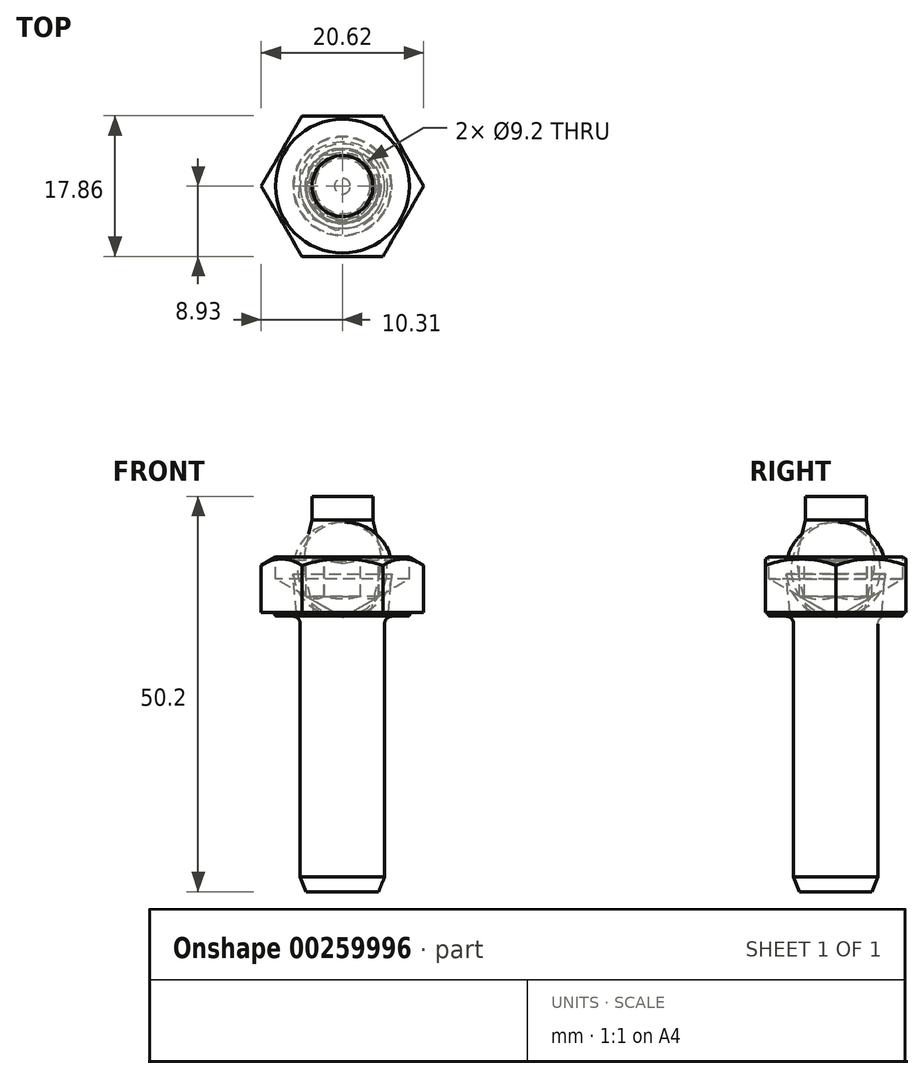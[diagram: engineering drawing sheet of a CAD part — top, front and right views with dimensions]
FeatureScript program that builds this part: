
annotation { "Feature Type Name" : "Feature", "Feature Type Description" : "" }
export const myFeature = defineFeature(function(context is Context, id is Id, definition is map)
    precondition{}
    {
        {
            var Q0;
            Q0=qCreatedBy(makeId("Front.planeOp"),FACE);
            var sketch = newSketch(context, id + "F0", { "sketchPlane" : qUnion([Q0])});
            skLineSegment(sketch, "E0", {"start": v(0, 0) * mm, "end": v(0, 0.42) * mm, "construction": true});
            skLineSegment(sketch, "E1", {"start": v(4.6, 7.5) * mm, "end": v(8.5, 7.5) * mm});
            skLineSegment(sketch, "E2", {"start": v(10.5, 6.35) * mm, "end": v(10.5, 0.5) * mm});
            skLineSegment(sketch, "E3", {"start": v(8.5, 0) * mm, "end": v(5.36, 0) * mm});
            skPoint(sketch, "E4.visualSharp", {"position": v(10.5, 7.5) * mm});
            skLineSegment(sketch, "E5", {"start": v(4.6, 7.5) * mm, "end": v(4.6, 2.5) * mm});
            skLineSegment(sketch, "E6", {"start": v(4.6, 2.5) * mm, "end": v(1, 0.42) * mm});
            skLineSegment(sketch, "E7", {"start": v(1, 0.42) * mm, "end": v(0, 0.42) * mm});
            skLineSegment(sketch, "E8", {"start": v(0, 0.42) * mm, "end": v(0, 0) * mm});
            skLineSegment(sketch, "E9", {"start": v(8.5, 7.5) * mm, "end": v(10.5, 6.35) * mm});
            skLineSegment(sketch, "E10", {"start": v(8.5, 0) * mm, "end": v(8.63, 0.5) * mm});
            skLineSegment(sketch, "E11", {"start": v(8.63, 0.5) * mm, "end": v(10.5, 0.5) * mm});
            skLineSegment(sketch, "E12", {"start": v(0, 0) * mm, "end": v(0, -35) * mm});
            skLineSegment(sketch, "E13", {"start": v(5.36, -33.13) * mm, "end": v(5.36, 0) * mm});
            skLineSegment(sketch, "E14", {"start": v(5.36, -33.13) * mm, "end": v(4.6, -35) * mm});
            skLineSegment(sketch, "E15", {"start": v(4.6, -35) * mm, "end": v(0, -35) * mm});
            skSolve(sketch);
        }
        {
            var Q0;
            Q0=qSketchRegion(id+"F0",true);
            var Q1;
            Q1=sQuery(id+"F0.wireOp",EDGE,"E8");
            revolve(context, id + "F1", {"entities" : qUnion([Q0]), "axis" : qUnion([Q1]), "revolveType" : RevolveType.FULL});
        }
        {
            var Q0;
            Q0=makeQuery(id+"F1.opRevolve","SWEPT_FACE",FACE,{"disambiguationData":[OSD([sQuery(id+"F0.wireOp",EDGE,"E1")])]});
            var sketch = newSketch(context, id + "F2", { "sketchPlane" : qUnion([Q0])});
            skCircle(sketch, "E16", {"center": v(0, 0) * mm, "radius": 4.6 * mm});
            skCircle(sketch, "E17.cCircle", {"center": v(0, 0) * mm, "radius": 4 * mm, "construction": true});
            skLineSegment(sketch, "E17.0", {"start": v(-2.3, 4) * mm, "end": v(2.3, 4) * mm});
            skLineSegment(sketch, "E17.1", {"start": v(2.3, 4) * mm, "end": v(4.62, 0) * mm});
            skLineSegment(sketch, "E17.2", {"start": v(4.62, 0) * mm, "end": v(2.3, -4) * mm});
            skLineSegment(sketch, "E17.3", {"start": v(2.3, -4) * mm, "end": v(-2.3, -4) * mm});
            skLineSegment(sketch, "E17.4", {"start": v(-2.3, -4) * mm, "end": v(-4.62, 0) * mm});
            skLineSegment(sketch, "E17.5", {"start": v(-4.62, 0) * mm, "end": v(-2.3, 4) * mm});
            skPoint(sketch, "E17.0.midPoint", {"position": v(0, 4) * mm});
            skSolve(sketch);
        }
        {
            var Q0;
            {var subQ0=sQuery(id+"F2.wireOp",EDGE,"E17.1");var subQ1=sQuery(id+"F2.wireOp",EDGE,"E16");var subQ2=makeQuery(id+"F2.imprint","INTERSECT",VERTEX,{"disambiguationData":[OD(0.0)],"derivedFrom":[subQ1,subQ0]});Q0=makeQuery(id+"F2.imprint","IMPRINT",FACE,{"disambiguationData":[TD([[makeQuery(id+"F2.imprint","IMPRINT",EDGE,{"disambiguationData":[TD([[subQ2,1.0]])],"derivedFrom":subQ1}),1.0]])]});}
            var Q1;
            {var subQ0=sQuery(id+"F2.wireOp",EDGE,"E17.1");var subQ1=sQuery(id+"F2.wireOp",EDGE,"E16");var subQ2=makeQuery(id+"F2.imprint","INTERSECT",VERTEX,{"disambiguationData":[OD(0.0)],"derivedFrom":[subQ1,subQ0]});Q1=makeQuery(id+"F2.imprint","IMPRINT",FACE,{"disambiguationData":[TD([[makeQuery(id+"F2.imprint","IMPRINT",EDGE,{"disambiguationData":[TD([[subQ2,-1.0]])],"derivedFrom":subQ1}),-1.0]])]});}
            var Q2;
            {var subQ0=sQuery(id+"F2.wireOp",EDGE,"E17.0");var subQ1=sQuery(id+"F2.wireOp",EDGE,"E16");var subQ2=makeQuery(id+"F2.imprint","INTERSECT",VERTEX,{"disambiguationData":[OD(0.0)],"derivedFrom":[subQ1,subQ0]});Q2=makeQuery(id+"F2.imprint","IMPRINT",FACE,{"disambiguationData":[TD([[makeQuery(id+"F2.imprint","IMPRINT",EDGE,{"disambiguationData":[TD([[subQ2,-1.0]])],"derivedFrom":subQ1}),1.0]])]});}
            var Q3;
            {var subQ0=sQuery(id+"F2.wireOp",EDGE,"E17.0");var subQ1=sQuery(id+"F2.wireOp",EDGE,"E16");var subQ2=makeQuery(id+"F2.imprint","INTERSECT",VERTEX,{"disambiguationData":[OD(1.0)],"derivedFrom":[subQ1,subQ0]});Q3=makeQuery(id+"F2.imprint","IMPRINT",FACE,{"disambiguationData":[TD([[makeQuery(id+"F2.imprint","IMPRINT",EDGE,{"disambiguationData":[TD([[subQ2,-1.0]])],"derivedFrom":subQ1}),-1.0]])]});}
            var Q4;
            {var subQ0=sQuery(id+"F2.wireOp",EDGE,"E17.5");var subQ1=sQuery(id+"F2.wireOp",EDGE,"E16");var subQ2=makeQuery(id+"F2.imprint","INTERSECT",VERTEX,{"disambiguationData":[OD(0.0)],"derivedFrom":[subQ1,subQ0]});Q4=makeQuery(id+"F2.imprint","IMPRINT",FACE,{"disambiguationData":[TD([[makeQuery(id+"F2.imprint","IMPRINT",EDGE,{"disambiguationData":[TD([[subQ2,-1.0]])],"derivedFrom":subQ1}),1.0]])]});}
            var Q5;
            {var subQ0=sQuery(id+"F2.wireOp",EDGE,"E17.5");var subQ1=sQuery(id+"F2.wireOp",EDGE,"E16");var subQ2=makeQuery(id+"F2.imprint","INTERSECT",VERTEX,{"disambiguationData":[OD(1.0)],"derivedFrom":[subQ1,subQ0]});Q5=makeQuery(id+"F2.imprint","IMPRINT",FACE,{"disambiguationData":[TD([[makeQuery(id+"F2.imprint","IMPRINT",EDGE,{"disambiguationData":[TD([[subQ2,-1.0]])],"derivedFrom":subQ1}),-1.0]])]});}
            var Q6;
            {var subQ0=sQuery(id+"F2.wireOp",EDGE,"E17.4");var subQ1=sQuery(id+"F2.wireOp",EDGE,"E16");var subQ2=makeQuery(id+"F2.imprint","INTERSECT",VERTEX,{"disambiguationData":[OD(0.0)],"derivedFrom":[subQ1,subQ0]});Q6=makeQuery(id+"F2.imprint","IMPRINT",FACE,{"disambiguationData":[TD([[makeQuery(id+"F2.imprint","IMPRINT",EDGE,{"disambiguationData":[TD([[subQ2,-1.0]])],"derivedFrom":subQ1}),1.0]])]});}
            var Q7;
            {var subQ0=sQuery(id+"F2.wireOp",EDGE,"E17.4");var subQ1=sQuery(id+"F2.wireOp",EDGE,"E16");var subQ2=makeQuery(id+"F2.imprint","INTERSECT",VERTEX,{"disambiguationData":[OD(1.0)],"derivedFrom":[subQ1,subQ0]});Q7=makeQuery(id+"F2.imprint","IMPRINT",FACE,{"disambiguationData":[TD([[makeQuery(id+"F2.imprint","IMPRINT",EDGE,{"disambiguationData":[TD([[subQ2,-1.0]])],"derivedFrom":subQ1}),-1.0]])]});}
            var Q8;
            {var subQ0=sQuery(id+"F2.wireOp",EDGE,"E17.3");var subQ1=sQuery(id+"F2.wireOp",EDGE,"E16");var subQ2=makeQuery(id+"F2.imprint","INTERSECT",VERTEX,{"disambiguationData":[OD(0.0)],"derivedFrom":[subQ1,subQ0]});Q8=makeQuery(id+"F2.imprint","IMPRINT",FACE,{"disambiguationData":[TD([[makeQuery(id+"F2.imprint","IMPRINT",EDGE,{"disambiguationData":[TD([[subQ2,-1.0]])],"derivedFrom":subQ1}),1.0]])]});}
            var Q9;
            {var subQ0=sQuery(id+"F2.wireOp",EDGE,"E17.3");var subQ1=sQuery(id+"F2.wireOp",EDGE,"E16");var subQ2=makeQuery(id+"F2.imprint","INTERSECT",VERTEX,{"disambiguationData":[OD(1.0)],"derivedFrom":[subQ1,subQ0]});Q9=makeQuery(id+"F2.imprint","IMPRINT",FACE,{"disambiguationData":[TD([[makeQuery(id+"F2.imprint","IMPRINT",EDGE,{"disambiguationData":[TD([[subQ2,-1.0]])],"derivedFrom":subQ1}),-1.0]])]});}
            var Q10;
            {var subQ0=sQuery(id+"F2.wireOp",EDGE,"E17.2");var subQ1=sQuery(id+"F2.wireOp",EDGE,"E16");var subQ2=makeQuery(id+"F2.imprint","INTERSECT",VERTEX,{"disambiguationData":[OD(0.0)],"derivedFrom":[subQ1,subQ0]});Q10=makeQuery(id+"F2.imprint","IMPRINT",FACE,{"disambiguationData":[TD([[makeQuery(id+"F2.imprint","IMPRINT",EDGE,{"disambiguationData":[TD([[subQ2,-1.0]])],"derivedFrom":subQ1}),1.0]])]});}
            var Q11;
            {var subQ0=sQuery(id+"F2.wireOp",EDGE,"E17.1");var subQ1=sQuery(id+"F2.wireOp",EDGE,"E16");var subQ2=makeQuery(id+"F2.imprint","INTERSECT",VERTEX,{"disambiguationData":[OD(1.0)],"derivedFrom":[subQ1,subQ0]});Q11=makeQuery(id+"F2.imprint","IMPRINT",FACE,{"disambiguationData":[TD([[makeQuery(id+"F2.imprint","IMPRINT",EDGE,{"disambiguationData":[TD([[subQ2,1.0]])],"derivedFrom":subQ1}),-1.0]])]});}
            var Q12;
            Q12=makeQuery(id+"F1.opRevolve","SWEPT_FACE",FACE,{"disambiguationData":[OSD([sQuery(id+"F0.wireOp",EDGE,"E6")])]});
            extrude(context, id + "F3", {"entities" : qUnion([Q0, Q1, Q2, Q3, Q4, Q5, Q6, Q7, Q8, Q9, Q10, Q11]), "operationType" : NewBodyOperationType.ADD, "endBound" : BoundingType.UP_TO_SURFACE, "oppositeDirection" : true, "endBoundEntityFace" : qUnion([Q12]), "depth" : 25 * mm});
        }
        {
            var Q0;
            Q0=makeQuery(id+"F3.boolean.opBoolean","MERGE",FACE,{"derivedFrom":[makeQuery(id+"F1.opRevolve","SWEPT_FACE",FACE,{"disambiguationData":[OSD([sQuery(id+"F0.wireOp",EDGE,"E1")])]}),makeQuery(id+"F3.opExtrude","CAP_FACE",FACE,{"disambiguationData":[OSD([sQuery(id+"F2.wireOp",EDGE,"axiUSiGf-8ymJ-Ezfh-tHsk-ULXXzRlxOoBz"),sQuery(id+"F2.wireOp",EDGE,"WrdyBTnM-XU54-uk96-2Sjo-h1HHDxb1zyqn"),sQuery(id+"F2.wireOp",EDGE,"7iNK7enz-fUzD-7EQp-KRCh-aPKnPlRcPdaK"),sQuery(id+"F2.wireOp",EDGE,"e7c95674-c634-4135-8625-61586754ee6a.1.0"),sQuery(id+"F2.wireOp",EDGE,"e7c95674-c634-4135-8625-61586754ee6a.1.1"),sQuery(id+"F2.wireOp",EDGE,"e7c95674-c634-4135-8625-61586754ee6a.1.2"),sQuery(id+"F2.wireOp",EDGE,"e7c95674-c634-4135-8625-61586754ee6a.2.0"),sQuery(id+"F2.wireOp",EDGE,"e7c95674-c634-4135-8625-61586754ee6a.2.1"),sQuery(id+"F2.wireOp",EDGE,"e7c95674-c634-4135-8625-61586754ee6a.2.2"),sQuery(id+"F2.wireOp",EDGE,"e7c95674-c634-4135-8625-61586754ee6a.3.0"),sQuery(id+"F2.wireOp",EDGE,"e7c95674-c634-4135-8625-61586754ee6a.3.1"),sQuery(id+"F2.wireOp",EDGE,"e7c95674-c634-4135-8625-61586754ee6a.3.2"),sQuery(id+"F2.wireOp",EDGE,"e7c95674-c634-4135-8625-61586754ee6a.4.0"),sQuery(id+"F2.wireOp",EDGE,"e7c95674-c634-4135-8625-61586754ee6a.4.1"),sQuery(id+"F2.wireOp",EDGE,"e7c95674-c634-4135-8625-61586754ee6a.4.2"),sQuery(id+"F2.wireOp",EDGE,"e7c95674-c634-4135-8625-61586754ee6a.5.0"),sQuery(id+"F2.wireOp",EDGE,"e7c95674-c634-4135-8625-61586754ee6a.5.1"),sQuery(id+"F2.wireOp",EDGE,"e7c95674-c634-4135-8625-61586754ee6a.5.2"),sQuery(id+"F2.wireOp",EDGE,"c34f7dbc-1fd9-48ae-9599-0fb72b0d65de.filletArc"),sQuery(id+"F2.wireOp",EDGE,"5fecc0f4-c57f-42b8-a97f-f8fbf54cf4db.filletArc"),sQuery(id+"F2.wireOp",EDGE,"b077568f-b672-48a6-a184-fa18c1575088.filletArc"),sQuery(id+"F2.wireOp",EDGE,"4c4ba650-eb3b-40a6-a5b6-7d0bcd232093.filletArc"),sQuery(id+"F2.wireOp",EDGE,"b016cc09-0b8d-437b-9508-1d7630c9d4ff.filletArc"),sQuery(id+"F2.wireOp",EDGE,"d5479cb3-145b-41e2-b586-5ab3f6452500.filletArc"),sQuery(id+"F2.wireOp",EDGE,"E16")])],"isStart":true})]});
            var sketch = newSketch(context, id + "F4", { "sketchPlane" : qUnion([Q0])});
            skCircle(sketch, "E18", {"center": v(0, 0) * mm, "radius": 4.75 * mm});
            skSolve(sketch);
        }
        {
            var Q0;
            Q0=qSketchRegion(id+"F4",true);
            extrude(context, id + "F5", {"entities" : qUnion([Q0]), "operationType" : NewBodyOperationType.REMOVE, "oppositeDirection" : true, "depth" : 1 * mm, "hasDraft" : true, "draftAngle" : 80 * degree, "draftPullDirection" : true});
        }
        {
            var Q0;
            {var subQ0=sQuery(id+"F2.wireOp",EDGE,"E16");Q0=makeQuery(id+"F3.boolean.opBoolean","MERGE",FACE,{"derivedFrom":[makeQuery(id+"F1.opRevolve","SWEPT_FACE",FACE,{"disambiguationData":[OSD([sQuery(id+"F0.wireOp",EDGE,"E1")])]}),makeQuery(id+"F3.opExtrude","CAP_FACE",FACE,{"disambiguationData":[OSD([subQ0,sQuery(id+"F2.wireOp",EDGE,"E17.1")])],"isStart":true}),makeQuery(id+"F3.opExtrude","CAP_FACE",FACE,{"disambiguationData":[OSD([subQ0,sQuery(id+"F2.wireOp",EDGE,"E17.0")])],"isStart":true}),makeQuery(id+"F3.opExtrude","CAP_FACE",FACE,{"disambiguationData":[OSD([subQ0,sQuery(id+"F2.wireOp",EDGE,"E17.5")])],"isStart":true}),makeQuery(id+"F3.opExtrude","CAP_FACE",FACE,{"disambiguationData":[OSD([subQ0,sQuery(id+"F2.wireOp",EDGE,"E17.4")])],"isStart":true}),makeQuery(id+"F3.opExtrude","CAP_FACE",FACE,{"disambiguationData":[OSD([subQ0,sQuery(id+"F2.wireOp",EDGE,"E17.3")])],"isStart":true}),makeQuery(id+"F3.opExtrude","CAP_FACE",FACE,{"disambiguationData":[OSD([subQ0,sQuery(id+"F2.wireOp",EDGE,"E17.2")])],"isStart":true})]});}
            var sketch = newSketch(context, id + "F6", { "sketchPlane" : qUnion([Q0])});
            skCircle(sketch, "E19.cCircle", {"center": v(0, 0) * mm, "radius": 8.93 * mm, "construction": true});
            skLineSegment(sketch, "E19.0", {"start": v(-5.15, 8.93) * mm, "end": v(5.15, 8.93) * mm});
            skLineSegment(sketch, "E19.1", {"start": v(5.15, 8.93) * mm, "end": v(10.3, 0) * mm});
            skLineSegment(sketch, "E19.2", {"start": v(10.3, 0) * mm, "end": v(5.15, -8.93) * mm});
            skLineSegment(sketch, "E19.3", {"start": v(5.15, -8.92) * mm, "end": v(-5.15, -8.93) * mm});
            skLineSegment(sketch, "E19.4", {"start": v(-5.15, -8.93) * mm, "end": v(-10.3, 0) * mm});
            skLineSegment(sketch, "E19.5", {"start": v(-10.3, 0) * mm, "end": v(-5.15, 8.93) * mm});
            skPoint(sketch, "E19.0.midPoint", {"position": v(0, 8.93) * mm});
            skCircle(sketch, "E20", {"center": v(0, 0) * mm, "radius": 12.96 * mm});
            skSolve(sketch);
        }
        {
            var Q0;
            Q0 = qSketchRegion(id + "F6", true);
            extrude(context, id + "F7", {"entities" : qUnion([Q0]), "operationType" : NewBodyOperationType.REMOVE, "endBound" : BoundingType.THROUGH_ALL, "oppositeDirection" : true, "depth" : 25 * mm});
        }
        {
            var Q0;
            Q0=qCreatedBy(makeId("Front.planeOp"),FACE);
            var sketch = newSketch(context, id + "F8", { "sketchPlane" : qUnion([Q0])});
            skLineSegment(sketch, "E21", {"start": v(0, 0) * mm, "end": v(0, 15.2) * mm, "construction": true});
            skLineSegment(sketch, "E22", {"start": v(0, 15.2) * mm, "end": v(3.87, 15.2) * mm});
            skLineSegment(sketch, "E23", {"start": v(3.87, 15.2) * mm, "end": v(3.87, 12.2) * mm});
            skLineSegment(sketch, "E24", {"start": v(3.87, 12.2) * mm, "end": v(4.68, 8.72) * mm});
            skLineSegment(sketch, "E25", {"start": v(3.5, 0) * mm, "end": v(0, 0) * mm});
            skLineSegment(sketch, "E26", {"start": v(0, 15.2) * mm, "end": v(0, 0) * mm});
            skLineSegment(sketch, "E27", {"start": v(3.5, 0) * mm, "end": v(4.68, 5.12) * mm});
            skArc(sketch, "E28.filletArc", {"start": v(4.68, 5.12) * mm, "mid": v(4.88, 6.92) * mm, "end": v(4.68, 8.72) * mm});
            skSolve(sketch);
        }
        {
            var Q0;
            Q0=qSketchRegion(id+"F8",true);
            var Q1;
            Q1=sQuery(id+"F8.wireOp",EDGE,"E26");
            revolve(context, id + "F9", {"entities" : qUnion([Q0]), "axis" : qUnion([Q1]), "revolveType" : RevolveType.FULL});
        }
        {
            var Q0;
            Q0=qCreatedBy(makeId("Front.planeOp"),FACE);
            var sketch = newSketch(context, id + "F10", { "sketchPlane" : qUnion([Q0])});
            skLineSegment(sketch, "E29", {"start": v(0, 0) * mm, "end": v(0, 7.03) * mm});
            skLineSegment(sketch, "E30", {"start": v(6.3, 5.39) * mm, "end": v(5.84, 0.45) * mm});
            skLineSegment(sketch, "E31", {"start": v(5.34, 0) * mm, "end": v(0, 0) * mm});
            skPoint(sketch, "E32.visualSharp", {"position": v(5.8, 0) * mm});
            skArc(sketch, "E32.filletArc", {"start": v(5.34, 0) * mm, "mid": v(5.68, 0.13) * mm, "end": v(5.84, 0.45) * mm});
            skLineSegment(sketch, "E33", {"start": v(0, 7.03) * mm, "end": v(0, 0) * mm, "construction": true});
            skLineSegment(sketch, "E34", {"start": v(0, 7.03) * mm, "end": v(1, 7.03) * mm});
            skLineSegment(sketch, "E35", {"start": v(1, 7.03) * mm, "end": v(4.25, 7.6) * mm});
            skLineSegment(sketch, "E36", {"start": v(4.25, 7.6) * mm, "end": v(5.74, 7.52) * mm});
            skArc(sketch, "E37.filletArc", {"start": v(6.3, 5.39) * mm, "mid": v(6.31, 6.26) * mm, "end": v(6.2, 7.12) * mm});
            skPoint(sketch, "E38.visualSharp", {"position": v(6.11, 7.5) * mm});
            skArc(sketch, "E38.filletArc", {"start": v(6.2, 7.12) * mm, "mid": v(6.04, 7.4) * mm, "end": v(5.74, 7.52) * mm});
            skLineSegment(sketch, "E39", {"start": v(6.3, 5.39) * mm, "end": v(6.35, 6) * mm, "construction": true});
            skSolve(sketch);
        }
        {
            var Q0;
            Q0=qSketchRegion(id+"F10",true);
            var Q1;
            Q1=sQuery(id+"F10.wireOp",EDGE,"E29");
            revolve(context, id + "F11", {"entities" : qUnion([Q0]), "axis" : qUnion([Q1]), "revolveType" : RevolveType.FULL});
        }
        {
            var Q0;
            Q0=makeQuery(id+"F1.opRevolve","SWEPT_EDGE",EDGE,{"disambiguationData":[OSD([sQuery(id+"F0.wireOp",EDGE,"E3"),sQuery(id+"F0.wireOp",EDGE,"E10")])]});
            var Q1;
            Q1=makeQuery(id+"F1.opRevolve","SWEPT_EDGE",EDGE,{"disambiguationData":[OSD([sQuery(id+"F0.wireOp",EDGE,"E10"),sQuery(id+"F0.wireOp",EDGE,"E11")])]});
            fillet(context, id + "F12", {"entities" : qUnion([Q0, Q1]), "radius" : 0.2 * mm, "tangentPropagation" : true, "allowEdgeOverflow" : false});
        }
        {
            var Q0;
            Q0=makeQuery(id+"F1.opRevolve","SWEPT_EDGE",EDGE,{"disambiguationData":[OSD([sQuery(id+"F0.wireOp",EDGE,"E3"),sQuery(id+"F0.wireOp",EDGE,"E13")])]});
            fillet(context, id + "F13", {"entities" : qUnion([Q0]), "radius" : 1 * mm, "tangentPropagation" : true, "allowEdgeOverflow" : false});
        }
    });
